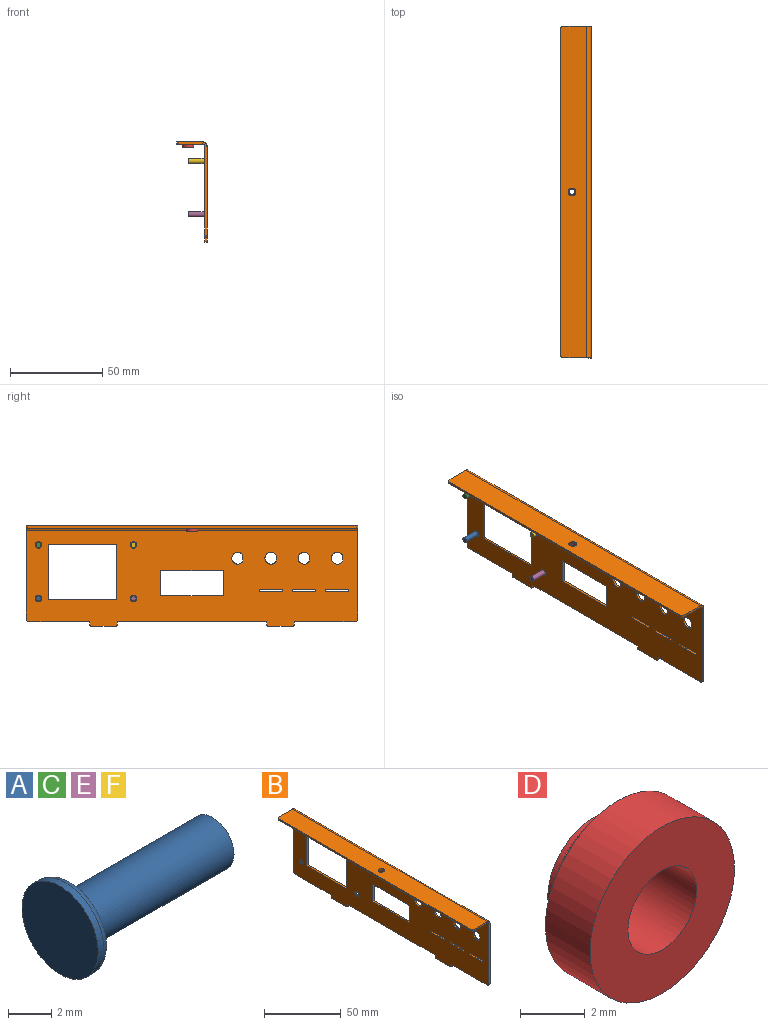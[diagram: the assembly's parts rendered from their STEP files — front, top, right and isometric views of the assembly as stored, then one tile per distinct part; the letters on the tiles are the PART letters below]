
ASSEMBLY  parts=6 mates=5
PART A: 8 faces, bbox 10x5.4x5.4 mm
  f0: cylinder r=1.4mm len=8.9mm, axis (-1,0,0), area 78.3mm2, adj f1,f2
  f1: plane 2.8x2.8mm, normal (1,0,0), area 6.2mm2, adj f0
  f2: plane 3x3mm, normal (1,0,0), area 0.9mm2, adj f0,f3
  f3: cylinder r=1.5mm len=3mm, axis (-1,0,0), area 3.3mm2, adj f2,f4
  f4: plane 4.25x4.25mm, normal (1,0,0), area 7.1mm2, adj f3,f5
  f5: torus R=2.12mm, axis (-1,0,0), area 8.7mm2, adj f4,f6
  f6: cylinder r=2.5mm len=5mm, axis (-1,0,0), area 5.9mm2, adj f5,f7
  f7: plane 5x5mm, normal (-1,0,0), area 19.6mm2, adj f6
PART B: 63 faces, bbox 16.4x180x54.3 mm
  f0: cylinder r=3.25mm len=6.5mm, axis (1,0,0), area 20.6mm2, adj f42,f43,f44
  f1: cylinder r=3.25mm len=6.5mm, axis (1,0,0), area 20.6mm2, adj f41,f43,f44
  f2: plane 12.5x1.2mm, normal (0,0,-1), area 15mm2, adj f3,f40,f43,f44
  f3: plane 1.25x1.2mm, normal (0,-1,0), area 1.5mm2, adj f2,f4,f43,f44
  f4: plane 12.5x1.2mm, normal (0,0,1), area 15mm2, adj f3,f40,f43,f44
  f5: plane 1.25x1.2mm, normal (0,1,0), area 1.5mm2, adj f6,f39,f43,f44
  f6: plane 12.5x1.2mm, normal (0,0,-1), area 15mm2, adj f5,f7,f43,f44
  f7: plane 1.25x1.2mm, normal (0,-1,0), area 1.5mm2, adj f6,f39,f43,f44
  f8: plane 12.5x1.2mm, normal (0,0,-1), area 15mm2, adj f9,f38,f43,f44
  f9: plane 1.25x1.2mm, normal (0,-1,0), area 1.5mm2, adj f8,f10,f43,f44
  f10: plane 12.5x1.2mm, normal (0,0,1), area 15mm2, adj f9,f38,f43,f44
  f11: plane 30x1.2mm, normal (0,1,0), area 36mm2, adj f12,f37,f43,f44
  f12: plane 37x1.2mm, normal (0,0,-1), area 44.4mm2, adj f11,f13,f43,f44
  f13: plane 30x1.2mm, normal (0,-1,0), area 36mm2, adj f12,f37,f43,f44
  f14: cylinder r=3.25mm len=6.5mm, axis (1,0,0), area 20.6mm2, adj f36,f43,f44
  f15: cylinder r=3.25mm len=6.5mm, axis (1,0,0), area 20.6mm2, adj f35,f43,f44
  f16: plane 34x1.2mm, normal (0,0,-1), area 40.8mm2, adj f17,f34,f43,f44
  f17: plane 13.65x1.2mm, normal (0,-1,0), area 16.4mm2, adj f16,f18,f43,f44
  f18: plane 34x1.2mm, normal (0,0,1), area 40.8mm2, adj f17,f34,f43,f44
  f19: plane 48.1x1.2mm, normal (0,-1,0), area 57.7mm2, adj f43,f44,f46,f60
  f20: plane 33x1.2mm, normal (0,0,-1), area 39.6mm2, adj f21,f43,f44,f46
  f21: plane 1.8x1.2mm, normal (0,-1,0), area 2.2mm2, adj f20,f43,f44,f47
  f22: plane 14x1.2mm, normal (0,0,-1), area 16.8mm2, adj f43,f44,f45,f47
  f23: plane 1.8x1.2mm, normal (0,1,0), area 2.2mm2, adj f24,f43,f44,f45
  f24: plane 81x1.2mm, normal (0,0,-1), area 97.2mm2, adj f23,f25,f43,f44
  f25: plane 1.8x1.2mm, normal (0,-1,0), area 2.2mm2, adj f24,f43,f44,f50
  f26: plane 14x1.2mm, normal (0,0,-1), area 16.8mm2, adj f43,f44,f49,f50
  f27: plane 1.8x1.2mm, normal (0,1,0), area 2.2mm2, adj f28,f43,f44,f49
  f28: plane 33x1.2mm, normal (0,0,-1), area 39.6mm2, adj f27,f43,f44,f48
  f29: plane 48.1x1.2mm, normal (0,1,0), area 57.7mm2, adj f43,f44,f48,f59
  f30: cylinder r=1.75mm len=3.5mm, axis (1,0,0), area 13.2mm2, adj f43,f44
  f31: cylinder r=1.75mm len=3.5mm, axis (1,0,0), area 13.2mm2, adj f43,f44
  f32: cylinder r=1.75mm len=3.5mm, axis (1,0,0), area 13.2mm2, adj f43,f44
  f33: cylinder r=1.75mm len=3.5mm, axis (1,0,0), area 13.2mm2, adj f43,f44
  f34: plane 13.65x1.2mm, normal (0,1,0), area 16.4mm2, adj f16,f18,f43,f44
  f35: plane 3.13x1.2mm, normal (0,1,0), area 3.8mm2, adj f15,f43,f44
  f36: plane 3.13x1.2mm, normal (0,1,0), area 3.8mm2, adj f14,f43,f44
  f37: plane 37x1.2mm, normal (0,0,1), area 44.4mm2, adj f11,f13,f43,f44
  f38: plane 1.25x1.2mm, normal (0,1,0), area 1.5mm2, adj f8,f10,f43,f44
  f39: plane 12.5x1.2mm, normal (0,0,1), area 15mm2, adj f5,f7,f43,f44
  f40: plane 1.25x1.2mm, normal (0,1,0), area 1.5mm2, adj f2,f4,f43,f44
  f41: plane 3.13x1.2mm, normal (0,1,0), area 3.8mm2, adj f1,f43,f44
  f42: plane 3.13x1.2mm, normal (0,1,0), area 3.8mm2, adj f0,f43,f44
  f43: plane 180x51.9mm, normal (1,0,0), area 7207mm2, adj f0,f1,f2,f3,f4,f5,f6,f7
  f44: plane 180x51.9mm, normal (-1,0,0), area 7207mm2, adj f0,f1,f2,f3,f4,f5,f6,f7
  f45: cylinder r=0.5mm len=1.2mm, axis (-1,0,0), area 0.9mm2, adj f22,f23,f43,f44
  f46: cylinder r=1.5mm len=1.5mm, axis (1,0,0), area 2.8mm2, adj f19,f20,f43,f44
  f47: cylinder r=0.5mm len=1.2mm, axis (1,0,0), area 0.9mm2, adj f21,f22,f43,f44
  f48: cylinder r=1.5mm len=1.5mm, axis (1,0,0), area 2.8mm2, adj f28,f29,f43,f44
  f49: cylinder r=0.5mm len=1.2mm, axis (-1,0,0), area 0.9mm2, adj f26,f27,f43,f44
  f50: cylinder r=0.5mm len=1.2mm, axis (1,0,0), area 0.9mm2, adj f25,f26,f43,f44
  f51: plane 178x1.2mm, normal (-1,0,0), area 213.6mm2, adj f55,f56,f57,f58
  f52: plane 13x1.2mm, normal (0,-1,0), area 15.6mm2, adj f55,f56,f57,f60
  f53: cylinder r=2.11mm len=4.22mm, axis (0,0,1), area 15.9mm2, adj f55,f56
  f54: plane 13x1.2mm, normal (0,1,0), area 15.6mm2, adj f55,f56,f58,f59
  f55: plane 180x14mm, normal (0,0,1), area 2505.6mm2, adj f51,f52,f53,f54,f57,f58,f61
  f56: plane 180x14mm, normal (0,0,-1), area 2505.6mm2, adj f51,f52,f53,f54,f57,f58,f62
  f57: cylinder r=1mm len=1.2mm, axis (0,0,-1), area 1.9mm2, adj f51,f52,f55,f56
  f58: cylinder r=1mm len=1.2mm, axis (0,0,-1), area 1.9mm2, adj f51,f54,f55,f56
  f59: plane 2.4x2.4mm, normal (0,1,0), area 3.4mm2, adj f29,f54,f61,f62
  f60: plane 2.4x2.4mm, normal (0,-1,0), area 3.4mm2, adj f19,f52,f61,f62
  f61: cylinder r=2.4mm len=180mm, axis (0,1,0), area 678.6mm2, adj f43,f55,f59,f60
  f62: cylinder r=1.2mm len=180mm, axis (0,1,0), area 339.3mm2, adj f44,f56,f59,f60
PART C: same geometry as A
PART D: 307 faces, bbox 6.3x3x6.3 mm
  f0: plane 5.01x5.01mm, normal (0,1,0), area 6.3mm2, adj f5,f6,f7,f8,f9,f10,f11,f12
  f1: plane 6.3x6.3mm, normal (0,1,0), area 12.3mm2, adj f3,f5,f6,f7,f8,f9,f10,f11
  f2: plane 6.3x6.3mm, normal (0,-1,0), area 24.1mm2, adj f3,f4
  f3: cylinder r=3.15mm len=6.3mm, axis (0,1,0), area 38.6mm2, adj f1,f2
  f4: cylinder r=1.5mm len=3mm, axis (0,1,0), area 28.2mm2, adj f2,f305
  f5: plane 0.5x0.1mm, normal (-0.89,0,0.45), area 0.1mm2, adj f0,f1,f6,f7
  f6: plane 0.5x0.1mm, normal (0.89,0,0.45), area 0.1mm2, adj f0,f1,f5,f8
  f7: plane 0.5x0.11mm, normal (0.91,0,0.41), area 0.1mm2, adj f0,f1,f5,f9
  f8: plane 0.5x0.11mm, normal (-0.91,0,0.41), area 0.1mm2, adj f0,f1,f6,f304
  f9: plane 0.5x0.1mm, normal (-0.87,0,0.49), area 0.1mm2, adj f0,f1,f7,f11
  f10: plane 0.5x0.1mm, normal (-0.85,0,0.52), area 0.1mm2, adj f0,f1,f11,f13
  f11: plane 0.5x0.11mm, normal (0.93,0,0.37), area 0.1mm2, adj f0,f1,f9,f10
  f12: plane 0.5x0.1mm, normal (-0.83,0,0.56), area 0.1mm2, adj f0,f1,f13,f15
  f13: plane 0.5x0.11mm, normal (0.94,0,0.34), area 0.1mm2, adj f0,f1,f10,f12
  f14: plane 0.5x0.09mm, normal (-0.81,0,0.59), area 0.1mm2, adj f0,f1,f15,f17
  f15: plane 0.5x0.11mm, normal (0.96,0,0.3), area 0.1mm2, adj f0,f1,f12,f14
  f16: plane 0.5x0.09mm, normal (-0.78,0,0.63), area 0.1mm2, adj f0,f1,f17,f19
  f17: plane 0.5x0.11mm, normal (0.97,0,0.26), area 0.1mm2, adj f0,f1,f14,f16
  f18: plane 0.5x0.09mm, normal (-0.75,0,0.66), area 0.1mm2, adj f0,f1,f19,f21
  f19: plane 0.5x0.11mm, normal (0.98,0,0.21), area 0.1mm2, adj f0,f1,f16,f18
  f20: plane 0.5x0.08mm, normal (-0.72,0,0.69), area 0.1mm2, adj f0,f1,f21,f23
  f21: plane 0.5x0.11mm, normal (0.98,0,0.17), area 0.1mm2, adj f0,f1,f18,f20
  f22: plane 0.5x0.08mm, normal (-0.69,0,0.72), area 0.1mm2, adj f0,f1,f23,f25
  f23: plane 0.5x0.12mm, normal (0.99,0,0.13), area 0.1mm2, adj f0,f1,f20,f22
  f24: plane 0.5x0.09mm, normal (-0.66,0,0.75), area 0.1mm2, adj f0,f1,f25,f27
  f25: plane 0.5x0.12mm, normal (1,0,0.09), area 0.1mm2, adj f0,f1,f22,f24
  f26: plane 0.5x0.09mm, normal (-0.63,0,0.77), area 0.1mm2, adj f0,f1,f27,f29
  f27: plane 0.5x0.12mm, normal (1,0,0.05), area 0.1mm2, adj f0,f1,f24,f26
  f28: plane 0.5x0.09mm, normal (-0.6,0,0.8), area 0.1mm2, adj f0,f1,f29,f31
  f29: plane 0.5x0.12mm, normal (1,0,0.01), area 0.1mm2, adj f0,f1,f26,f28
  f30: plane 0.5x0.1mm, normal (-0.57,0,0.82), area 0.1mm2, adj f0,f1,f31,f33
  f31: plane 0.5x0.12mm, normal (1,0,-0.04), area 0.1mm2, adj f0,f1,f28,f30
  f32: plane 0.5x0.1mm, normal (-0.53,0,0.85), area 0.1mm2, adj f0,f1,f33,f35
  f33: plane 0.5x0.12mm, normal (1,0,-0.08), area 0.1mm2, adj f0,f1,f30,f32
  f34: plane 0.5x0.1mm, normal (-0.49,0,0.87), area 0.1mm2, adj f0,f1,f35,f37
  f35: plane 0.5x0.12mm, normal (0.99,0,-0.12), area 0.1mm2, adj f0,f1,f32,f34
  f36: plane 0.5x0.1mm, normal (-0.46,0,0.89), area 0.1mm2, adj f0,f1,f37,f39
  f37: plane 0.5x0.12mm, normal (0.99,0,-0.16), area 0.1mm2, adj f0,f1,f34,f36
  f38: plane 0.5x0.11mm, normal (-0.42,0,0.91), area 0.1mm2, adj f0,f1,f39,f41
  f39: plane 0.5x0.11mm, normal (0.98,0,-0.2), area 0.1mm2, adj f0,f1,f36,f38
  f40: plane 0.5x0.11mm, normal (-0.38,0,0.92), area 0.1mm2, adj f0,f1,f41,f43
  f41: plane 0.5x0.11mm, normal (0.97,0,-0.24), area 0.1mm2, adj f0,f1,f38,f40
  f42: plane 0.5x0.11mm, normal (-0.34,0,0.94), area 0.1mm2, adj f0,f1,f43,f45
  f43: plane 0.5x0.11mm, normal (0.96,0,-0.28), area 0.1mm2, adj f0,f1,f40,f42
  f44: plane 0.5x0.11mm, normal (-0.3,0,0.95), area 0.1mm2, adj f0,f1,f45,f47
  f45: plane 0.5x0.11mm, normal (0.95,0,-0.32), area 0.1mm2, adj f0,f1,f42,f44
  f46: plane 0.5x0.11mm, normal (-0.26,0,0.96), area 0.1mm2, adj f0,f1,f47,f49
  f47: plane 0.5x0.11mm, normal (0.93,0,-0.36), area 0.1mm2, adj f0,f1,f44,f46
  f48: plane 0.5x0.11mm, normal (-0.22,0,0.98), area 0.1mm2, adj f0,f1,f49,f51
  f49: plane 0.5x0.11mm, normal (0.92,0,-0.4), area 0.1mm2, adj f0,f1,f46,f48
  f50: plane 0.5x0.11mm, normal (-0.18,0,0.98), area 0.1mm2, adj f0,f1,f51,f53
  f51: plane 0.5x0.1mm, normal (0.9,0,-0.44), area 0.1mm2, adj f0,f1,f48,f50
  f52: plane 0.5x0.12mm, normal (-0.14,0,0.99), area 0.1mm2, adj f0,f1,f53,f55
  f53: plane 0.5x0.1mm, normal (0.88,0,-0.48), area 0.1mm2, adj f0,f1,f50,f52
  f54: plane 0.5x0.12mm, normal (-0.1,0,1), area 0.1mm2, adj f0,f1,f55,f57
  f55: plane 0.5x0.1mm, normal (0.86,0,-0.51), area 0.1mm2, adj f0,f1,f52,f54
  f56: plane 0.5x0.12mm, normal (-0.06,0,1), area 0.1mm2, adj f0,f1,f57,f59
  f57: plane 0.5x0.1mm, normal (0.84,0,-0.55), area 0.1mm2, adj f0,f1,f54,f56
  f58: plane 0.5x0.12mm, normal (-0.01,0,1), area 0.1mm2, adj f0,f1,f59,f61
  f59: plane 0.5x0.09mm, normal (0.81,0,-0.58), area 0.1mm2, adj f0,f1,f56,f58
  f60: plane 0.5x0.12mm, normal (0.03,0,1), area 0.1mm2, adj f0,f1,f61,f63
  f61: plane 0.5x0.09mm, normal (0.79,0,-0.62), area 0.1mm2, adj f0,f1,f58,f60
  f62: plane 0.5x0.12mm, normal (0.07,0,1), area 0.1mm2, adj f0,f1,f63,f65
  f63: plane 0.5x0.09mm, normal (0.76,0,-0.65), area 0.1mm2, adj f0,f1,f60,f62
  f64: plane 0.5x0.12mm, normal (0.11,0,0.99), area 0.1mm2, adj f0,f1,f65,f67
  f65: plane 0.5x0.09mm, normal (0.73,0,-0.68), area 0.1mm2, adj f0,f1,f62,f64
  f66: plane 0.5x0.12mm, normal (0.15,0,0.99), area 0.1mm2, adj f0,f1,f67,f69
  f67: plane 0.5x0.08mm, normal (0.7,0,-0.71), area 0.1mm2, adj f0,f1,f64,f66
  f68: plane 0.5x0.11mm, normal (0.19,0,0.98), area 0.1mm2, adj f0,f1,f69,f71
  f69: plane 0.5x0.09mm, normal (0.67,0,-0.74), area 0.1mm2, adj f0,f1,f66,f68
  f70: plane 0.5x0.11mm, normal (0.23,0,0.97), area 0.1mm2, adj f0,f1,f71,f73
  f71: plane 0.5x0.09mm, normal (0.64,0,-0.77), area 0.1mm2, adj f0,f1,f68,f70
  f72: plane 0.5x0.11mm, normal (0.28,0,0.96), area 0.1mm2, adj f0,f1,f73,f75
  f73: plane 0.5x0.09mm, normal (0.61,0,-0.79), area 0.1mm2, adj f0,f1,f70,f72
  f74: plane 0.5x0.11mm, normal (0.32,0,0.95), area 0.1mm2, adj f0,f1,f75,f77
  f75: plane 0.5x0.1mm, normal (0.58,0,-0.82), area 0.1mm2, adj f0,f1,f72,f74
  f76: plane 0.5x0.11mm, normal (0.35,0,0.93), area 0.1mm2, adj f0,f1,f77,f79
  f77: plane 0.5x0.1mm, normal (0.54,0,-0.84), area 0.1mm2, adj f0,f1,f74,f76
  f78: plane 0.5x0.11mm, normal (0.39,0,0.92), area 0.1mm2, adj f0,f1,f79,f81
  f79: plane 0.5x0.1mm, normal (0.51,0,-0.86), area 0.1mm2, adj f0,f1,f76,f78
  f80: plane 0.5x0.11mm, normal (0.43,0,0.9), area 0.1mm2, adj f0,f1,f81,f83
  f81: plane 0.5x0.1mm, normal (0.47,0,-0.88), area 0.1mm2, adj f0,f1,f78,f80
  f82: plane 0.5x0.1mm, normal (0.47,0,0.88), area 0.1mm2, adj f0,f1,f83,f85
  f83: plane 0.5x0.11mm, normal (0.43,0,-0.9), area 0.1mm2, adj f0,f1,f80,f82
  f84: plane 0.5x0.1mm, normal (0.51,0,0.86), area 0.1mm2, adj f0,f1,f85,f87
  f85: plane 0.5x0.11mm, normal (0.39,0,-0.92), area 0.1mm2, adj f0,f1,f82,f84
  f86: plane 0.5x0.1mm, normal (0.54,0,0.84), area 0.1mm2, adj f0,f1,f87,f89
  f87: plane 0.5x0.11mm, normal (0.35,0,-0.93), area 0.1mm2, adj f0,f1,f84,f86
  f88: plane 0.5x0.1mm, normal (0.58,0,0.82), area 0.1mm2, adj f0,f1,f89,f91
  f89: plane 0.5x0.11mm, normal (0.32,0,-0.95), area 0.1mm2, adj f0,f1,f86,f88
  f90: plane 0.5x0.09mm, normal (0.61,0,0.79), area 0.1mm2, adj f0,f1,f91,f93
  f91: plane 0.5x0.11mm, normal (0.28,0,-0.96), area 0.1mm2, adj f0,f1,f88,f90
  f92: plane 0.5x0.09mm, normal (0.64,0,0.77), area 0.1mm2, adj f0,f1,f93,f95
  f93: plane 0.5x0.11mm, normal (0.23,0,-0.97), area 0.1mm2, adj f0,f1,f90,f92
  f94: plane 0.5x0.09mm, normal (0.67,0,0.74), area 0.1mm2, adj f0,f1,f95,f97
  f95: plane 0.5x0.11mm, normal (0.19,0,-0.98), area 0.1mm2, adj f0,f1,f92,f94
  f96: plane 0.5x0.08mm, normal (0.7,0,0.71), area 0.1mm2, adj f0,f1,f97,f99
  f97: plane 0.5x0.12mm, normal (0.15,0,-0.99), area 0.1mm2, adj f0,f1,f94,f96
  f98: plane 0.5x0.09mm, normal (0.73,0,0.68), area 0.1mm2, adj f0,f1,f99,f101
  f99: plane 0.5x0.12mm, normal (0.11,0,-0.99), area 0.1mm2, adj f0,f1,f96,f98
  f100: plane 0.5x0.09mm, normal (0.76,0,0.65), area 0.1mm2, adj f0,f1,f101,f103
  f101: plane 0.5x0.12mm, normal (0.07,0,-1), area 0.1mm2, adj f0,f1,f98,f100
  f102: plane 0.5x0.09mm, normal (0.79,0,0.62), area 0.1mm2, adj f0,f1,f103,f105
  f103: plane 0.5x0.12mm, normal (0.03,0,-1), area 0.1mm2, adj f0,f1,f100,f102
  f104: plane 0.5x0.09mm, normal (0.81,0,0.58), area 0.1mm2, adj f0,f1,f105,f107
  f105: plane 0.5x0.12mm, normal (-0.01,0,-1), area 0.1mm2, adj f0,f1,f102,f104
  f106: plane 0.5x0.1mm, normal (0.84,0,0.55), area 0.1mm2, adj f0,f1,f107,f109
  f107: plane 0.5x0.12mm, normal (-0.06,0,-1), area 0.1mm2, adj f0,f1,f104,f106
  f108: plane 0.5x0.1mm, normal (0.86,0,0.51), area 0.1mm2, adj f0,f1,f109,f111
  f109: plane 0.5x0.12mm, normal (-0.1,0,-1), area 0.1mm2, adj f0,f1,f106,f108
  f110: plane 0.5x0.1mm, normal (0.88,0,0.48), area 0.1mm2, adj f0,f1,f111,f113
  f111: plane 0.5x0.12mm, normal (-0.14,0,-0.99), area 0.1mm2, adj f0,f1,f108,f110
  f112: plane 0.5x0.1mm, normal (0.9,0,0.44), area 0.1mm2, adj f0,f1,f113,f115
  f113: plane 0.5x0.11mm, normal (-0.18,0,-0.98), area 0.1mm2, adj f0,f1,f110,f112
  f114: plane 0.5x0.11mm, normal (0.92,0,0.4), area 0.1mm2, adj f0,f1,f115,f117
  f115: plane 0.5x0.11mm, normal (-0.22,0,-0.98), area 0.1mm2, adj f0,f1,f112,f114
  f116: plane 0.5x0.11mm, normal (0.93,0,0.36), area 0.1mm2, adj f0,f1,f117,f119
  f117: plane 0.5x0.11mm, normal (-0.26,0,-0.96), area 0.1mm2, adj f0,f1,f114,f116
  f118: plane 0.5x0.11mm, normal (0.95,0,0.32), area 0.1mm2, adj f0,f1,f119,f121
  f119: plane 0.5x0.11mm, normal (-0.3,0,-0.95), area 0.1mm2, adj f0,f1,f116,f118
  f120: plane 0.5x0.11mm, normal (0.96,0,0.28), area 0.1mm2, adj f0,f1,f121,f123
  f121: plane 0.5x0.11mm, normal (-0.34,0,-0.94), area 0.1mm2, adj f0,f1,f118,f120
  f122: plane 0.5x0.11mm, normal (0.97,0,0.24), area 0.1mm2, adj f0,f1,f123,f125
  f123: plane 0.5x0.11mm, normal (-0.38,0,-0.92), area 0.1mm2, adj f0,f1,f120,f122
  f124: plane 0.5x0.11mm, normal (0.98,0,0.2), area 0.1mm2, adj f0,f1,f125,f127
  f125: plane 0.5x0.11mm, normal (-0.42,0,-0.91), area 0.1mm2, adj f0,f1,f122,f124
  f126: plane 0.5x0.12mm, normal (0.99,0,0.16), area 0.1mm2, adj f0,f1,f127,f129
  f127: plane 0.5x0.1mm, normal (-0.46,0,-0.89), area 0.1mm2, adj f0,f1,f124,f126
  f128: plane 0.5x0.12mm, normal (0.99,0,0.12), area 0.1mm2, adj f0,f1,f129,f131
  f129: plane 0.5x0.1mm, normal (-0.49,0,-0.87), area 0.1mm2, adj f0,f1,f126,f128
  f130: plane 0.5x0.12mm, normal (1,0,0.08), area 0.1mm2, adj f0,f1,f131,f133
  f131: plane 0.5x0.1mm, normal (-0.53,0,-0.85), area 0.1mm2, adj f0,f1,f128,f130
  f132: plane 0.5x0.12mm, normal (1,0,0.04), area 0.1mm2, adj f0,f1,f133,f135
  f133: plane 0.5x0.1mm, normal (-0.57,0,-0.82), area 0.1mm2, adj f0,f1,f130,f132
  f134: plane 0.5x0.12mm, normal (1,0,-0.01), area 0.1mm2, adj f0,f1,f135,f137
  f135: plane 0.5x0.09mm, normal (-0.6,0,-0.8), area 0.1mm2, adj f0,f1,f132,f134
  f136: plane 0.5x0.12mm, normal (1,0,-0.05), area 0.1mm2, adj f0,f1,f137,f139
  f137: plane 0.5x0.09mm, normal (-0.63,0,-0.77), area 0.1mm2, adj f0,f1,f134,f136
  f138: plane 0.5x0.12mm, normal (1,0,-0.09), area 0.1mm2, adj f0,f1,f139,f141
  f139: plane 0.5x0.09mm, normal (-0.66,0,-0.75), area 0.1mm2, adj f0,f1,f136,f138
  f140: plane 0.5x0.12mm, normal (0.99,0,-0.13), area 0.1mm2, adj f0,f1,f141,f143
  f141: plane 0.5x0.08mm, normal (-0.69,0,-0.72), area 0.1mm2, adj f0,f1,f138,f140
  f142: plane 0.5x0.11mm, normal (0.98,0,-0.17), area 0.1mm2, adj f0,f1,f143,f145
  f143: plane 0.5x0.08mm, normal (-0.72,0,-0.69), area 0.1mm2, adj f0,f1,f140,f142
  f144: plane 0.5x0.11mm, normal (0.98,0,-0.21), area 0.1mm2, adj f0,f1,f145,f147
  f145: plane 0.5x0.09mm, normal (-0.75,0,-0.66), area 0.1mm2, adj f0,f1,f142,f144
  f146: plane 0.5x0.11mm, normal (0.97,0,-0.26), area 0.1mm2, adj f0,f1,f147,f149
  f147: plane 0.5x0.09mm, normal (-0.78,0,-0.63), area 0.1mm2, adj f0,f1,f144,f146
  f148: plane 0.5x0.11mm, normal (0.96,0,-0.3), area 0.1mm2, adj f0,f1,f149,f151
  f149: plane 0.5x0.09mm, normal (-0.81,0,-0.59), area 0.1mm2, adj f0,f1,f146,f148
  f150: plane 0.5x0.11mm, normal (0.94,0,-0.34), area 0.1mm2, adj f0,f1,f151,f153
  f151: plane 0.5x0.1mm, normal (-0.83,0,-0.56), area 0.1mm2, adj f0,f1,f148,f150
  f152: plane 0.5x0.11mm, normal (0.93,0,-0.37), area 0.1mm2, adj f0,f1,f153,f155
  f153: plane 0.5x0.1mm, normal (-0.85,0,-0.52), area 0.1mm2, adj f0,f1,f150,f152
  f154: plane 0.5x0.11mm, normal (0.91,0,-0.41), area 0.1mm2, adj f0,f1,f155,f157
  f155: plane 0.5x0.1mm, normal (-0.87,0,-0.49), area 0.1mm2, adj f0,f1,f152,f154
  f156: plane 0.5x0.1mm, normal (0.89,0,-0.45), area 0.1mm2, adj f0,f1,f157,f159
  f157: plane 0.5x0.1mm, normal (-0.89,0,-0.45), area 0.1mm2, adj f0,f1,f154,f156
  f158: plane 0.5x0.1mm, normal (0.87,0,-0.49), area 0.1mm2, adj f0,f1,f159,f161
  f159: plane 0.5x0.11mm, normal (-0.91,0,-0.41), area 0.1mm2, adj f0,f1,f156,f158
  f160: plane 0.5x0.1mm, normal (0.85,0,-0.52), area 0.1mm2, adj f0,f1,f161,f163
  f161: plane 0.5x0.11mm, normal (-0.93,0,-0.37), area 0.1mm2, adj f0,f1,f158,f160
  f162: plane 0.5x0.1mm, normal (0.83,0,-0.56), area 0.1mm2, adj f0,f1,f163,f165
  f163: plane 0.5x0.11mm, normal (-0.94,0,-0.34), area 0.1mm2, adj f0,f1,f160,f162
  f164: plane 0.5x0.09mm, normal (0.81,0,-0.59), area 0.1mm2, adj f0,f1,f165,f167
  f165: plane 0.5x0.11mm, normal (-0.96,0,-0.3), area 0.1mm2, adj f0,f1,f162,f164
  f166: plane 0.5x0.09mm, normal (0.78,0,-0.63), area 0.1mm2, adj f0,f1,f167,f169
  f167: plane 0.5x0.11mm, normal (-0.97,0,-0.26), area 0.1mm2, adj f0,f1,f164,f166
  f168: plane 0.5x0.09mm, normal (0.75,0,-0.66), area 0.1mm2, adj f0,f1,f169,f171
  f169: plane 0.5x0.11mm, normal (-0.98,0,-0.21), area 0.1mm2, adj f0,f1,f166,f168
  f170: plane 0.5x0.08mm, normal (0.72,0,-0.69), area 0.1mm2, adj f0,f1,f171,f173
  f171: plane 0.5x0.11mm, normal (-0.98,0,-0.17), area 0.1mm2, adj f0,f1,f168,f170
  f172: plane 0.5x0.08mm, normal (0.69,0,-0.72), area 0.1mm2, adj f0,f1,f173,f175
  f173: plane 0.5x0.12mm, normal (-0.99,0,-0.13), area 0.1mm2, adj f0,f1,f170,f172
  f174: plane 0.5x0.09mm, normal (0.66,0,-0.75), area 0.1mm2, adj f0,f1,f175,f177
  f175: plane 0.5x0.12mm, normal (-1,0,-0.09), area 0.1mm2, adj f0,f1,f172,f174
  f176: plane 0.5x0.09mm, normal (0.63,0,-0.77), area 0.1mm2, adj f0,f1,f177,f179
  f177: plane 0.5x0.12mm, normal (-1,0,-0.05), area 0.1mm2, adj f0,f1,f174,f176
  f178: plane 0.5x0.09mm, normal (0.6,0,-0.8), area 0.1mm2, adj f0,f1,f179,f181
  f179: plane 0.5x0.12mm, normal (-1,0,-0.01), area 0.1mm2, adj f0,f1,f176,f178
  f180: plane 0.5x0.1mm, normal (0.57,0,-0.82), area 0.1mm2, adj f0,f1,f181,f183
  f181: plane 0.5x0.12mm, normal (-1,0,0.04), area 0.1mm2, adj f0,f1,f178,f180
  f182: plane 0.5x0.1mm, normal (0.53,0,-0.85), area 0.1mm2, adj f0,f1,f183,f185
  f183: plane 0.5x0.12mm, normal (-1,0,0.08), area 0.1mm2, adj f0,f1,f180,f182
  f184: plane 0.5x0.1mm, normal (0.49,0,-0.87), area 0.1mm2, adj f0,f1,f185,f187
  f185: plane 0.5x0.12mm, normal (-0.99,0,0.12), area 0.1mm2, adj f0,f1,f182,f184
  f186: plane 0.5x0.1mm, normal (0.46,0,-0.89), area 0.1mm2, adj f0,f1,f187,f189
  f187: plane 0.5x0.12mm, normal (-0.99,0,0.16), area 0.1mm2, adj f0,f1,f184,f186
  f188: plane 0.5x0.11mm, normal (0.42,0,-0.91), area 0.1mm2, adj f0,f1,f189,f191
  f189: plane 0.5x0.11mm, normal (-0.98,0,0.2), area 0.1mm2, adj f0,f1,f186,f188
  f190: plane 0.5x0.11mm, normal (0.38,0,-0.92), area 0.1mm2, adj f0,f1,f191,f193
  f191: plane 0.5x0.11mm, normal (-0.97,0,0.24), area 0.1mm2, adj f0,f1,f188,f190
  f192: plane 0.5x0.11mm, normal (0.34,0,-0.94), area 0.1mm2, adj f0,f1,f193,f195
  f193: plane 0.5x0.11mm, normal (-0.96,0,0.28), area 0.1mm2, adj f0,f1,f190,f192
  f194: plane 0.5x0.11mm, normal (0.3,0,-0.95), area 0.1mm2, adj f0,f1,f195,f197
  f195: plane 0.5x0.11mm, normal (-0.95,0,0.32), area 0.1mm2, adj f0,f1,f192,f194
  f196: plane 0.5x0.11mm, normal (0.26,0,-0.96), area 0.1mm2, adj f0,f1,f197,f199
  f197: plane 0.5x0.11mm, normal (-0.93,0,0.36), area 0.1mm2, adj f0,f1,f194,f196
  f198: plane 0.5x0.11mm, normal (0.22,0,-0.98), area 0.1mm2, adj f0,f1,f199,f201
  f199: plane 0.5x0.11mm, normal (-0.92,0,0.4), area 0.1mm2, adj f0,f1,f196,f198
  f200: plane 0.5x0.11mm, normal (0.18,0,-0.98), area 0.1mm2, adj f0,f1,f201,f203
  f201: plane 0.5x0.1mm, normal (-0.9,0,0.44), area 0.1mm2, adj f0,f1,f198,f200
  f202: plane 0.5x0.12mm, normal (0.14,0,-0.99), area 0.1mm2, adj f0,f1,f203,f205
  f203: plane 0.5x0.1mm, normal (-0.88,0,0.48), area 0.1mm2, adj f0,f1,f200,f202
  f204: plane 0.5x0.12mm, normal (0.1,0,-1), area 0.1mm2, adj f0,f1,f205,f207
  f205: plane 0.5x0.1mm, normal (-0.86,0,0.51), area 0.1mm2, adj f0,f1,f202,f204
  f206: plane 0.5x0.12mm, normal (0.06,0,-1), area 0.1mm2, adj f0,f1,f207,f209
  f207: plane 0.5x0.1mm, normal (-0.84,0,0.55), area 0.1mm2, adj f0,f1,f204,f206
  f208: plane 0.5x0.12mm, normal (0.01,0,-1), area 0.1mm2, adj f0,f1,f209,f211
  f209: plane 0.5x0.09mm, normal (-0.81,0,0.58), area 0.1mm2, adj f0,f1,f206,f208
  f210: plane 0.5x0.12mm, normal (-0.03,0,-1), area 0.1mm2, adj f0,f1,f211,f213
  f211: plane 0.5x0.09mm, normal (-0.79,0,0.62), area 0.1mm2, adj f0,f1,f208,f210
  f212: plane 0.5x0.12mm, normal (-0.07,0,-1), area 0.1mm2, adj f0,f1,f213,f215
  f213: plane 0.5x0.09mm, normal (-0.76,0,0.65), area 0.1mm2, adj f0,f1,f210,f212
  f214: plane 0.5x0.12mm, normal (-0.11,0,-0.99), area 0.1mm2, adj f0,f1,f215,f217
  f215: plane 0.5x0.09mm, normal (-0.73,0,0.68), area 0.1mm2, adj f0,f1,f212,f214
  f216: plane 0.5x0.12mm, normal (-0.15,0,-0.99), area 0.1mm2, adj f0,f1,f217,f219
  f217: plane 0.5x0.08mm, normal (-0.7,0,0.71), area 0.1mm2, adj f0,f1,f214,f216
  f218: plane 0.5x0.11mm, normal (-0.19,0,-0.98), area 0.1mm2, adj f0,f1,f219,f221
  f219: plane 0.5x0.09mm, normal (-0.67,0,0.74), area 0.1mm2, adj f0,f1,f216,f218
  f220: plane 0.5x0.11mm, normal (-0.23,0,-0.97), area 0.1mm2, adj f0,f1,f221,f223
  f221: plane 0.5x0.09mm, normal (-0.64,0,0.77), area 0.1mm2, adj f0,f1,f218,f220
  f222: plane 0.5x0.11mm, normal (-0.28,0,-0.96), area 0.1mm2, adj f0,f1,f223,f225
  f223: plane 0.5x0.09mm, normal (-0.61,0,0.79), area 0.1mm2, adj f0,f1,f220,f222
  f224: plane 0.5x0.11mm, normal (-0.32,0,-0.95), area 0.1mm2, adj f0,f1,f225,f227
  f225: plane 0.5x0.1mm, normal (-0.58,0,0.82), area 0.1mm2, adj f0,f1,f222,f224
  f226: plane 0.5x0.11mm, normal (-0.35,0,-0.93), area 0.1mm2, adj f0,f1,f227,f229
  f227: plane 0.5x0.1mm, normal (-0.54,0,0.84), area 0.1mm2, adj f0,f1,f224,f226
  f228: plane 0.5x0.11mm, normal (-0.39,0,-0.92), area 0.1mm2, adj f0,f1,f229,f231
  f229: plane 0.5x0.1mm, normal (-0.51,0,0.86), area 0.1mm2, adj f0,f1,f226,f228
  f230: plane 0.5x0.11mm, normal (-0.43,0,-0.9), area 0.1mm2, adj f0,f1,f231,f233
  f231: plane 0.5x0.1mm, normal (-0.47,0,0.88), area 0.1mm2, adj f0,f1,f228,f230
  f232: plane 0.5x0.1mm, normal (-0.47,0,-0.88), area 0.1mm2, adj f0,f1,f233,f235
  f233: plane 0.5x0.11mm, normal (-0.43,0,0.9), area 0.1mm2, adj f0,f1,f230,f232
  f234: plane 0.5x0.1mm, normal (-0.51,0,-0.86), area 0.1mm2, adj f0,f1,f235,f237
  f235: plane 0.5x0.11mm, normal (-0.39,0,0.92), area 0.1mm2, adj f0,f1,f232,f234
  f236: plane 0.5x0.1mm, normal (-0.54,0,-0.84), area 0.1mm2, adj f0,f1,f237,f239
  f237: plane 0.5x0.11mm, normal (-0.35,0,0.93), area 0.1mm2, adj f0,f1,f234,f236
  f238: plane 0.5x0.1mm, normal (-0.58,0,-0.82), area 0.1mm2, adj f0,f1,f239,f241
  f239: plane 0.5x0.11mm, normal (-0.32,0,0.95), area 0.1mm2, adj f0,f1,f236,f238
  f240: plane 0.5x0.09mm, normal (-0.61,0,-0.79), area 0.1mm2, adj f0,f1,f241,f243
  f241: plane 0.5x0.11mm, normal (-0.28,0,0.96), area 0.1mm2, adj f0,f1,f238,f240
  f242: plane 0.5x0.09mm, normal (-0.64,0,-0.77), area 0.1mm2, adj f0,f1,f243,f245
  f243: plane 0.5x0.11mm, normal (-0.23,0,0.97), area 0.1mm2, adj f0,f1,f240,f242
  f244: plane 0.5x0.09mm, normal (-0.67,0,-0.74), area 0.1mm2, adj f0,f1,f245,f247
  f245: plane 0.5x0.11mm, normal (-0.19,0,0.98), area 0.1mm2, adj f0,f1,f242,f244
  f246: plane 0.5x0.08mm, normal (-0.7,0,-0.71), area 0.1mm2, adj f0,f1,f247,f249
  f247: plane 0.5x0.12mm, normal (-0.15,0,0.99), area 0.1mm2, adj f0,f1,f244,f246
  f248: plane 0.5x0.09mm, normal (-0.73,0,-0.68), area 0.1mm2, adj f0,f1,f249,f251
  f249: plane 0.5x0.12mm, normal (-0.11,0,0.99), area 0.1mm2, adj f0,f1,f246,f248
  f250: plane 0.5x0.09mm, normal (-0.76,0,-0.65), area 0.1mm2, adj f0,f1,f251,f253
  f251: plane 0.5x0.12mm, normal (-0.07,0,1), area 0.1mm2, adj f0,f1,f248,f250
  f252: plane 0.5x0.09mm, normal (-0.79,0,-0.62), area 0.1mm2, adj f0,f1,f253,f255
  f253: plane 0.5x0.12mm, normal (-0.03,0,1), area 0.1mm2, adj f0,f1,f250,f252
  f254: plane 0.5x0.09mm, normal (-0.81,0,-0.58), area 0.1mm2, adj f0,f1,f255,f257
  f255: plane 0.5x0.12mm, normal (0.01,0,1), area 0.1mm2, adj f0,f1,f252,f254
  f256: plane 0.5x0.1mm, normal (-0.84,0,-0.55), area 0.1mm2, adj f0,f1,f257,f259
  f257: plane 0.5x0.12mm, normal (0.06,0,1), area 0.1mm2, adj f0,f1,f254,f256
  f258: plane 0.5x0.1mm, normal (-0.86,0,-0.51), area 0.1mm2, adj f0,f1,f259,f261
  f259: plane 0.5x0.12mm, normal (0.1,0,1), area 0.1mm2, adj f0,f1,f256,f258
  f260: plane 0.5x0.1mm, normal (-0.88,0,-0.48), area 0.1mm2, adj f0,f1,f261,f263
  f261: plane 0.5x0.12mm, normal (0.14,0,0.99), area 0.1mm2, adj f0,f1,f258,f260
  f262: plane 0.5x0.1mm, normal (-0.9,0,-0.44), area 0.1mm2, adj f0,f1,f263,f265
  f263: plane 0.5x0.11mm, normal (0.18,0,0.98), area 0.1mm2, adj f0,f1,f260,f262
  f264: plane 0.5x0.11mm, normal (-0.92,0,-0.4), area 0.1mm2, adj f0,f1,f265,f267
  f265: plane 0.5x0.11mm, normal (0.22,0,0.98), area 0.1mm2, adj f0,f1,f262,f264
  f266: plane 0.5x0.11mm, normal (-0.93,0,-0.36), area 0.1mm2, adj f0,f1,f267,f269
  f267: plane 0.5x0.11mm, normal (0.26,0,0.96), area 0.1mm2, adj f0,f1,f264,f266
  f268: plane 0.5x0.11mm, normal (-0.95,0,-0.32), area 0.1mm2, adj f0,f1,f269,f271
  f269: plane 0.5x0.11mm, normal (0.3,0,0.95), area 0.1mm2, adj f0,f1,f266,f268
  f270: plane 0.5x0.11mm, normal (-0.96,0,-0.28), area 0.1mm2, adj f0,f1,f271,f273
  f271: plane 0.5x0.11mm, normal (0.34,0,0.94), area 0.1mm2, adj f0,f1,f268,f270
  f272: plane 0.5x0.11mm, normal (-0.97,0,-0.24), area 0.1mm2, adj f0,f1,f273,f275
  f273: plane 0.5x0.11mm, normal (0.38,0,0.92), area 0.1mm2, adj f0,f1,f270,f272
  f274: plane 0.5x0.11mm, normal (-0.98,0,-0.2), area 0.1mm2, adj f0,f1,f275,f277
  f275: plane 0.5x0.11mm, normal (0.42,0,0.91), area 0.1mm2, adj f0,f1,f272,f274
  f276: plane 0.5x0.12mm, normal (-0.99,0,-0.16), area 0.1mm2, adj f0,f1,f277,f279
  f277: plane 0.5x0.1mm, normal (0.46,0,0.89), area 0.1mm2, adj f0,f1,f274,f276
  f278: plane 0.5x0.12mm, normal (-0.99,0,-0.12), area 0.1mm2, adj f0,f1,f279,f281
  f279: plane 0.5x0.1mm, normal (0.49,0,0.87), area 0.1mm2, adj f0,f1,f276,f278
  f280: plane 0.5x0.12mm, normal (-1,0,-0.08), area 0.1mm2, adj f0,f1,f281,f283
  f281: plane 0.5x0.1mm, normal (0.53,0,0.85), area 0.1mm2, adj f0,f1,f278,f280
  f282: plane 0.5x0.12mm, normal (-1,0,-0.04), area 0.1mm2, adj f0,f1,f283,f285
  f283: plane 0.5x0.1mm, normal (0.57,0,0.82), area 0.1mm2, adj f0,f1,f280,f282
  f284: plane 0.5x0.12mm, normal (-1,0,0.01), area 0.1mm2, adj f0,f1,f285,f287
  f285: plane 0.5x0.09mm, normal (0.6,0,0.8), area 0.1mm2, adj f0,f1,f282,f284
  f286: plane 0.5x0.12mm, normal (-1,0,0.05), area 0.1mm2, adj f0,f1,f287,f289
  f287: plane 0.5x0.09mm, normal (0.63,0,0.77), area 0.1mm2, adj f0,f1,f284,f286
  f288: plane 0.5x0.12mm, normal (-1,0,0.09), area 0.1mm2, adj f0,f1,f289,f291
  f289: plane 0.5x0.09mm, normal (0.66,0,0.75), area 0.1mm2, adj f0,f1,f286,f288
  f290: plane 0.5x0.12mm, normal (-0.99,0,0.13), area 0.1mm2, adj f0,f1,f291,f293
  f291: plane 0.5x0.08mm, normal (0.69,0,0.72), area 0.1mm2, adj f0,f1,f288,f290
  f292: plane 0.5x0.11mm, normal (-0.98,0,0.17), area 0.1mm2, adj f0,f1,f293,f295
  f293: plane 0.5x0.08mm, normal (0.72,0,0.69), area 0.1mm2, adj f0,f1,f290,f292
  f294: plane 0.5x0.11mm, normal (-0.98,0,0.21), area 0.1mm2, adj f0,f1,f295,f297
  f295: plane 0.5x0.09mm, normal (0.75,0,0.66), area 0.1mm2, adj f0,f1,f292,f294
  f296: plane 0.5x0.11mm, normal (-0.97,0,0.26), area 0.1mm2, adj f0,f1,f297,f299
  f297: plane 0.5x0.09mm, normal (0.78,0,0.63), area 0.1mm2, adj f0,f1,f294,f296
  f298: plane 0.5x0.11mm, normal (-0.96,0,0.3), area 0.1mm2, adj f0,f1,f299,f301
  f299: plane 0.5x0.09mm, normal (0.81,0,0.59), area 0.1mm2, adj f0,f1,f296,f298
  f300: plane 0.5x0.11mm, normal (-0.94,0,0.34), area 0.1mm2, adj f0,f1,f301,f303
  f301: plane 0.5x0.1mm, normal (0.83,0,0.56), area 0.1mm2, adj f0,f1,f298,f300
  f302: plane 0.5x0.11mm, normal (-0.93,0,0.37), area 0.1mm2, adj f0,f1,f303,f304
  f303: plane 0.5x0.1mm, normal (0.85,0,0.52), area 0.1mm2, adj f0,f1,f300,f302
  f304: plane 0.5x0.1mm, normal (0.87,0,0.49), area 0.1mm2, adj f0,f1,f8,f302
  f305: plane 4x4mm, normal (0,1,0), area 5.5mm2, adj f4,f306
  f306: cylinder r=2mm len=4mm, axis (0,-1,0), area 6.9mm2, adj f0,f305
PART E: same geometry as A
PART F: same geometry as A
PLACE A rot(axis=(0,0,1),180deg) t=(56.2,83.25,14.2)mm
PLACE B at identity fixed
PLACE C rot(axis=(0,0,1),180deg) t=(56.2,83.25,43.2)mm
PLACE D rot(axis=(1,0,0),90deg) t=(45.8,0,52.3)mm
PLACE E rot(axis=(0,0,1),180deg) t=(56.2,31.75,14.2)mm
PLACE F rot(axis=(0,0,1),180deg) t=(56.2,31.75,43.2)mm
MATE fastened C.f0 <-> B.f31  axis (1,0,0) through (56.2,83.25,43.2)mm
MATE fastened F.f0 <-> B.f30  axis (1,0,0) through (56.2,31.75,43.2)mm
MATE fastened D.f3 <-> B.f53  axis (0,0,1) through (45.8,0,52.3)mm
MATE fastened E.f0 <-> B.f33  axis (1,0,0) through (56.2,31.75,14.2)mm
MATE fastened A.f0 <-> B.f32  axis (1,0,0) through (56.2,83.25,14.2)mm
